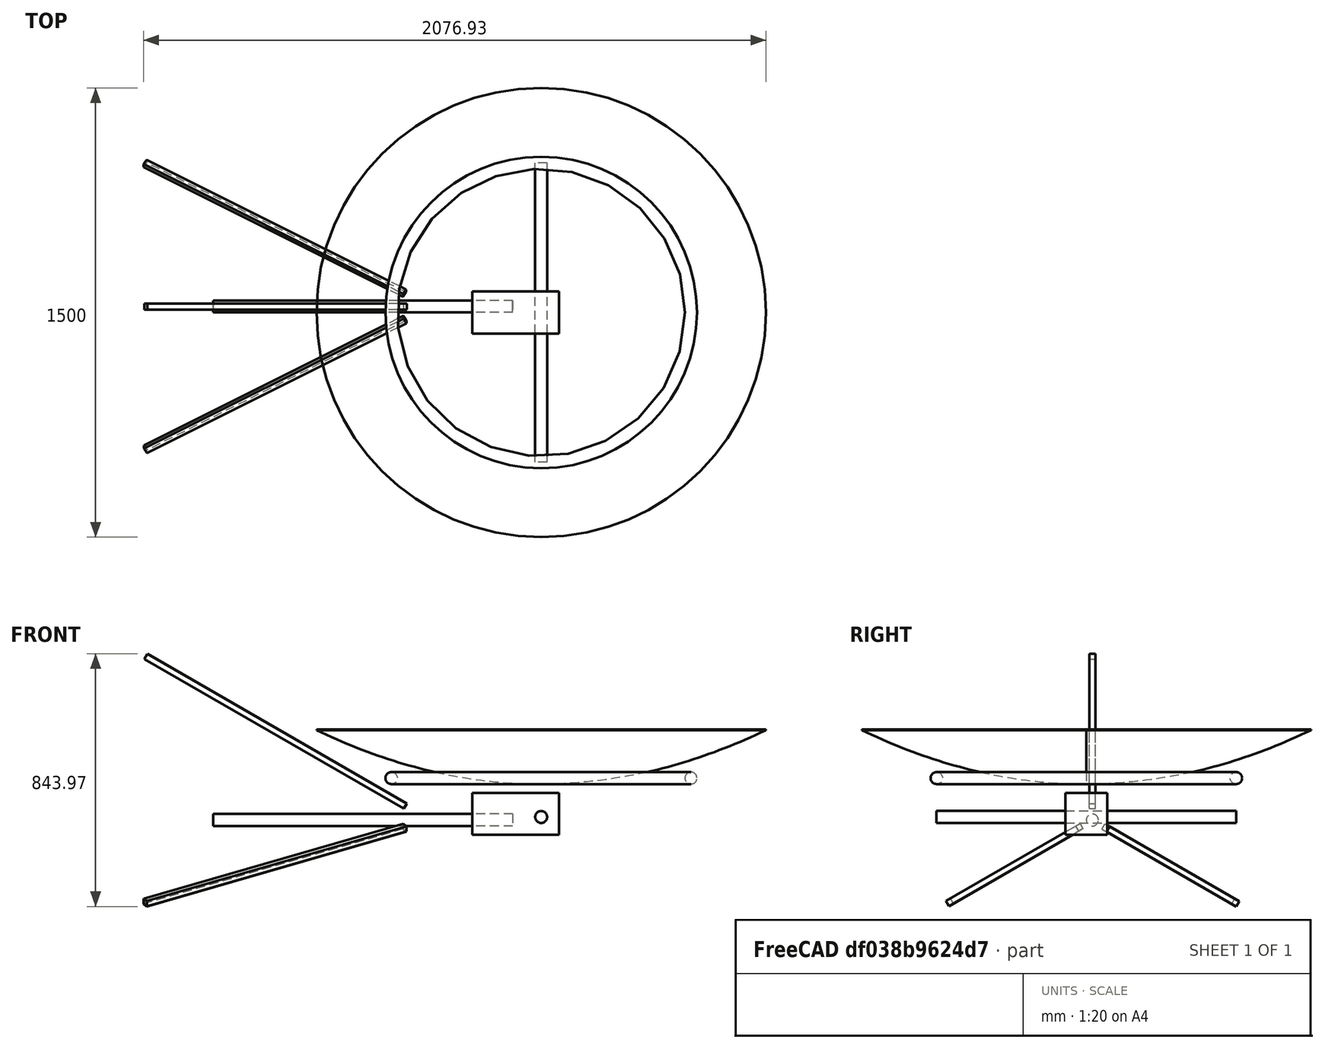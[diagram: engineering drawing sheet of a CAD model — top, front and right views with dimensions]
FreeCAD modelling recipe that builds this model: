
FCSTD DOCUMENT  (FreeCAD 0.19R)
Label: dish
License: All rights reserved
LicenseURL: http://en.wikipedia.org/wiki/All_rights_reserved
objects: Sketcher::SketchObject×3, PartDesign::Body×3, Part::Box×3, PartDesign::Revolution×2, Part::Cylinder×2, PartDesign::Pad×1, Mesh::Feature×1
note: 17 computed .brp shape members not serialized (recipe doc carries the construction recipe); baked Part::Feature solids carry a one-line shape summary decoded from their .brp

FEATURE [Sketcher::SketchObject] Sketch
  MapMode = 5
  Placement = pos=(0,0,0) rot=(1,0,0;1.5708rad)
  Support = -> [XZ_Plane]
  sketch-geometry (6):
    g0: ArcOfParabola CenterX=0 CenterY=0 CenterZ=0 NormalX=0 NormalY=0 NormalZ=1 Focal=781.25 AngleXU=1.5708 StartAngle=-750 EndAngle=0
    g1: GeomPoint X=0 Y=781.25 Z=0
    g2: LineSegment [constr] StartX=0 StartY=0 StartZ=0 EndX=0 EndY=781.25 EndZ=0
    g3: ArcOfParabola CenterX=0 CenterY=3 CenterZ=0 NormalX=0 NormalY=0 NormalZ=1 Focal=781.25 AngleXU=1.5708 StartAngle=-750 EndAngle=0
    g4: LineSegment StartX=750 StartY=180 StartZ=0 EndX=750 EndY=183 EndZ=0
    g5: LineSegment StartX=0 StartY=3 StartZ=0 EndX=0 EndY=0 EndZ=0
  constraints (18):
    c: InternalAlignment(g1,g0)
    c: Coincident(g1,g2)
    c: Coincident(g0,g2)
    c: Coincident(g0,g-1)
    c: PointOnObject(g1,g-2)
    c: PointOnObject(g0,g2)
    c: Equal(g0,g3) = 750
    c: PointOnObject(g3,g2)
    c: DistanceY(g3) = 183
    c: DistanceY(g0) = 180
    c: Coincident(g4,g0)
    c: Coincident(g4,g3)
    c: Parallel(g4,g2)
    c: PointOnObject(g3,g2)
    c: Coincident(g5,g3)
    c: Coincident(g5,g0)
    c: Equal(g5,g4)
    c: DistanceX(g0) = 750
FEATURE [Sketcher::SketchObject] Sketch001
  MapMode = 5
  Placement = pos=(0,0,0) rot=(1,0,0;1.5708rad)
  Support = -> [XZ_Plane001]
  sketch-geometry (1):
    g0: Circle CenterX=500 CenterY=20 CenterZ=0 NormalX=0 NormalY=0 NormalZ=1 AngleXU=0 Radius=20
  constraints (3):
    c: Diameter(g0) = 40
    c: DistanceX(g-1,g0) = 500
    c: DistanceY(g0) = 20
FEATURE [PartDesign::Revolution] Revolution001
  Angle = 360
  Axis = (0,-2e-16,1)
  Base = (0,0,0)
  Placement = pos=(0,0,0) rot=(1,0,0;1.5708rad)
  Profile = -> Sketch
  ReferenceAxis = -> Sketch [V_Axis]
  Reversed = true
FEATURE [PartDesign::Body] Body
  Group = -> [Sketch,Revolution001]
  Origin = -> Origin
  Tip = -> Revolution001
FEATURE [PartDesign::Revolution] Revolution
  Angle = 360
  Axis = (0,2e-16,1)
  Base = (0,0,0)
  Placement = pos=(0,0,0) rot=(1,0,0;1.5708rad)
  Profile = -> Sketch001
  ReferenceAxis = -> Sketch001 [V_Axis]
  Reversed = true
FEATURE [PartDesign::Body] Body001
  Group = -> [Sketch001,Revolution]
  Origin = -> Origin001
  Tip = -> Revolution
FEATURE [Sketcher::SketchObject] Sketch002
  MapMode = 5
  Placement = pos=(0,0,0) rot=(0.57735,0.57735,0.57735;2.0944rad)
  Support = -> [YZ_Plane002]
  sketch-geometry (4):
    g0: LineSegment StartX=-70 StartY=-170 StartZ=0 EndX=70 EndY=-170 EndZ=0
    g1: LineSegment StartX=70 StartY=-170 StartZ=0 EndX=70 EndY=-30 EndZ=0
    g2: LineSegment StartX=70 StartY=-30 StartZ=0 EndX=-70 EndY=-30 EndZ=0
    g3: LineSegment StartX=-70 StartY=-30 StartZ=0 EndX=-70 EndY=-170 EndZ=0
  constraints (14):
    c: Coincident(g0,g1)
    c: Coincident(g1,g2)
    c: Coincident(g2,g3)
    c: Coincident(g3,g0)
    c: Horizontal(g0)
    c: Horizontal(g2)
    c: Vertical(g1)
    c: Vertical(g3)
    c: Equal(g0,g3)
    c: Equal(g3,g2)
    c: Equal(g2,g1)
    c: DistanceX(g0,g0) = 140
    c: DistanceX(g0) = -70
    c: DistanceY(g0) = -170
FEATURE [PartDesign::Pad] Pad
  Length = 60
  Length2 = 230
  Midplane = true
  Placement = pos=(0,0,0) rot=(0.57735,0.57735,0.57735;2.0944rad)
  Profile = -> Sketch002
  Type = 4
FEATURE [PartDesign::Body] Body002
  Group = -> [Sketch002,Pad]
  Origin = -> Origin002
  Tip = -> Pad
FEATURE [Part::Cylinder] Cylinder
  Angle = 360
  AttacherType = Attacher::AttachEngine3D
  Height = 1000
  Placement = pos=(-95,20,-120) rot=(0,-1,0;1.5708rad)
  Radius = 20
FEATURE [Part::Cylinder] Cylinder001
  Angle = 360
  AttacherType = Attacher::AttachEngine3D
  Height = 1000
  Placement = pos=(0,-500,-110) rot=(-1,0,0;1.5708rad)
  Radius = 20
FEATURE [Mesh::Feature] topholder
  Placement = pos=(-480,20,-120) rot=(0.250563,0.935113,0.250563;1.63783rad)
FEATURE [Part::Box] Box  label="Cube"
  AttacherType = Attacher::AttachEngine3D
  Height = 1000
  Length = 20
  Placement = pos=(-458.407,10,-82.3205) rot=(0,-1,0;1.0472rad)
  Width = 20
FEATURE [Part::Box] Box001  label="Cube001"
  AttacherType = Attacher::AttachEngine3D
  Height = 1000
  Length = 20
  Placement = pos=(-459.747,-21.1186,-132.345) rot=(0.707107,0.353553,-0.612372;3.14159rad)
  Width = 20
FEATURE [Part::Box] Box002  label="Cube002"
  AttacherType = Attacher::AttachEngine3D
  Height = 1000
  Length = 20
  Placement = pos=(-460.907,52.2372,-150.311) rot=(-0.447214,-0.894427,0;1.82348rad)
  Width = 20
